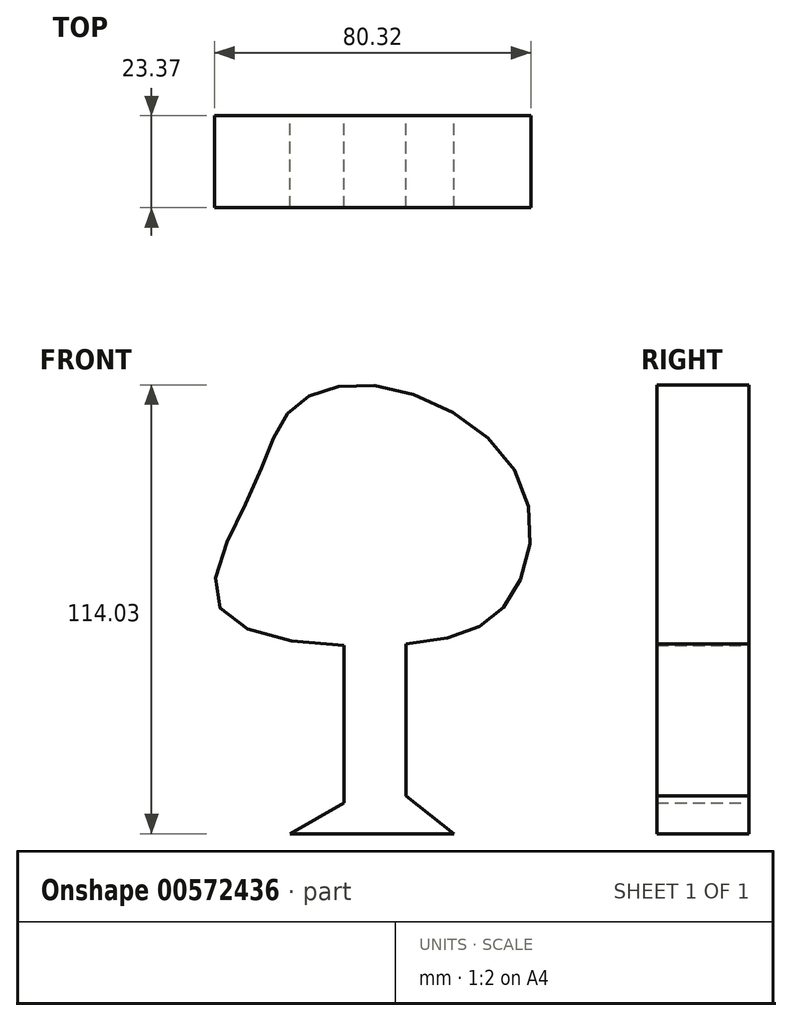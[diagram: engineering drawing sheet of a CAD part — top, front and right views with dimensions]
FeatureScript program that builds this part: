
annotation { "Feature Type Name" : "Feature", "Feature Type Description" : "" }
export const myFeature = defineFeature(function(context is Context, id is Id, definition is map)
    precondition{}
    {
        {
            var Q0;
            Q0=qCreatedBy(makeId("Front.planeOp"),FACE);
            var sketch = newSketch(context, id + "F0", { "sketchPlane" : qUnion([Q0])});
            skLineSegment(sketch, "E0", {"start": v(15.77, 22.48) * mm, "end": v(15.77, -31.24) * mm});
            skLineSegment(sketch, "E1", {"start": v(15.77, -31.24) * mm, "end": v(28.03, -40.88) * mm});
            skLineSegment(sketch, "E2", {"start": v(28.03, -40.88) * mm, "end": v(-2.92, -40.88) * mm});
            skLineSegment(sketch, "E3", {"start": v(0, 22.48) * mm, "end": v(0, -33) * mm});
            skLineSegment(sketch, "E4", {"start": v(0, -33) * mm, "end": v(-13.72, -40.88) * mm});
            skLineSegment(sketch, "E5", {"start": v(-13.72, -40.88) * mm, "end": v(-2.92, -40.88) * mm});
            skLineSegment(sketch, "E6", {"start": v(0, 22.48) * mm, "end": v(15.77, 22.48) * mm});
            skFitSpline(sketch, "E7", {"points": [v(15.77, 7.3) * mm, v(41.76, 18.1) * mm, v(45.26, 47.89) * mm, v(12.85, 72.13) * mm, v(-12.26, 68.04) * mm, v(-22.78, 47.6) * mm, v(-31.54, 16.64) * mm, v(15.77, 7.3) * mm]});
            skSolve(sketch);
        }
        {
            var Q0;
            Q0 = qSketchRegion(id + "F0", true);
            extrude(context, id + "F1", {"entities" : qUnion([Q0]), "depth" : 23.37 * mm, "offsetDistance" : 25.4 * mm});
        }
    });
